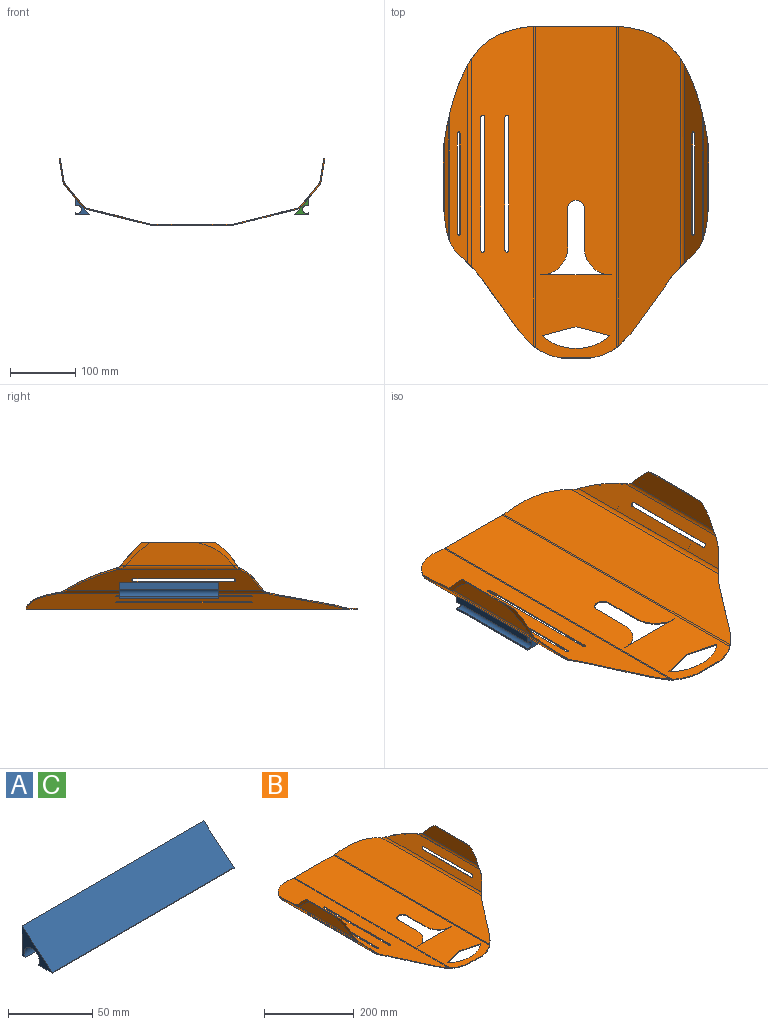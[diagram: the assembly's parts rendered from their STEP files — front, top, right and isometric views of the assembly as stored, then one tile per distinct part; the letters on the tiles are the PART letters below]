
ASSEMBLY  parts=3 mates=2
PART A: 8 faces, bbox 152.4x25.4x21.7 mm
  f0: plane 152.4x2.76mm, normal (0,0,-1), area 420mm2, adj f2,f5,f6,f7
  f1: plane 152.4x11.65mm, normal (0,0,-1), area 1774.8mm2, adj f4,f5,f6,f7
  f2: plane 152.4x21.72mm, normal (0,1,0), area 3310.1mm2, adj f0,f3,f5,f6
  f3: plane 152.4x25.4mm, normal (0,-0.64,0.77), area 5053.2mm2, adj f2,f4,f5,f6
  f4: plane 152.4x0.41mm, normal (0,-1,0), area 61.9mm2, adj f1,f3,f5,f6
  f5: plane 25.4x21.72mm, normal (1,0,0), area 179.1mm2, adj f0,f1,f2,f3,f4,f7
  f6: plane 25.4x21.72mm, normal (-1,0,0), area 179.1mm2, adj f0,f1,f2,f3,f4,f7
  f7: cylinder r=6.35mm len=152.4mm, axis (1,0,0), area 4053.7mm2, adj f0,f1,f5,f6
PART B: 60 faces, bbox 406.5x508.7x101.6 mm
  f0: plane 508.66x125.18mm, normal (0,0,-1), area 56761.7mm2, adj f16,f17,f18,f29,f30,f31,f32,f33
  f1: plane 508.66x125.18mm, normal (0,0,1), area 56761.7mm2, adj f6,f17,f28,f29,f30,f31,f32,f33
  f2: plane 298.37x32.29mm, normal (0.77,0,-0.64), area 9580.6mm2, adj f20,f21,f30,f32,f38,f39,f40,f41
  f3: plane 301.73x32.29mm, normal (-0.77,0,0.64), area 9787.3mm2, adj f25,f26,f30,f32,f38,f39,f40,f41
  f4: plane 301.73x32.29mm, normal (0.77,0,0.64), area 9787.3mm2, adj f8,f9,f31,f33,f34,f35,f36,f37
  f5: plane 298.37x32.29mm, normal (-0.77,0,-0.64), area 9580.6mm2, adj f13,f14,f31,f33,f34,f35,f36,f37
  f6: cylinder r=11.11mm len=491.86mm, axis (0,1,0), area 1338.6mm2, adj f1,f7,f31,f33
  f7: plane 489.51x95.87mm, normal (0.24,0,0.97), area 38384.7mm2, adj f6,f8,f31,f33,f52,f53,f54,f55
  f8: cylinder r=11.11mm len=316.99mm, axis (0,1,0), area 2156.1mm2, adj f4,f7,f31,f33
  f9: cylinder r=11.11mm len=194.91mm, axis (0,1,0), area 1096.4mm2, adj f4,f10,f31,f33
  f10: plane 177.21x34.42mm, normal (0.99,0,0.16), area 5197.5mm2, adj f9,f11,f31,f33
  f11: plane 112.31x1.72mm, normal (0,0,1), area 152.9mm2, adj f10,f12,f31,f33
  f12: plane 163.81x34.68mm, normal (-0.99,0,-0.16), area 4502.2mm2, adj f11,f13,f31,f33
  f13: cylinder r=12.7mm len=186.54mm, axis (0,1,0), area 1173.8mm2, adj f5,f12,f31,f33
  f14: cylinder r=12.7mm len=316.01mm, axis (0,1,0), area 2446.8mm2, adj f5,f15,f31,f33
  f15: plane 489.15x95.87mm, normal (-0.24,0,-0.97), area 38315.9mm2, adj f14,f16,f31,f33,f52,f53,f54,f55
  f16: cylinder r=12.7mm len=491.86mm, axis (0,1,0), area 1529.3mm2, adj f0,f15,f31,f33
  f17: plane 44.52x1.59mm, normal (0,-1,0), area 70.7mm2, adj f0,f1,f32,f33
  f18: cylinder r=12.7mm len=491.86mm, axis (0,1,0), area 1529.3mm2, adj f0,f19,f30,f32
  f19: plane 489.15x95.87mm, normal (0.24,0,-0.97), area 40960mm2, adj f18,f20,f30,f32
  f20: cylinder r=12.7mm len=316.01mm, axis (0,1,0), area 2446.8mm2, adj f2,f19,f30,f32
  f21: cylinder r=12.7mm len=186.54mm, axis (0,1,0), area 1173.8mm2, adj f2,f22,f30,f32
  f22: plane 163.81x34.68mm, normal (0.99,0,-0.16), area 4502.2mm2, adj f21,f23,f30,f32
  f23: plane 112.31x1.72mm, normal (0,0,1), area 152.9mm2, adj f22,f24,f30,f32
  f24: plane 177.21x34.42mm, normal (-0.99,0,0.16), area 5197.5mm2, adj f23,f25,f30,f32
  f25: cylinder r=11.11mm len=194.91mm, axis (0,1,0), area 1096.4mm2, adj f3,f24,f30,f32
  f26: cylinder r=11.11mm len=316.99mm, axis (0,1,0), area 2156.1mm2, adj f3,f27,f30,f32
  f27: plane 489.51x95.87mm, normal (-0.24,0,0.97), area 41028.7mm2, adj f26,f28,f30,f32
  f28: cylinder r=11.11mm len=491.86mm, axis (0,1,0), area 1338.6mm2, adj f1,f27,f30,f32
  f29: plane 121.22x1.59mm, normal (0,1,0), area 192.4mm2, adj f0,f1,f30,f31
  f30: extruded ~189.8x142.59mm, area 795.1mm2, adj f0,f1,f2,f3,f18,f19,f20,f21
  f31: extruded ~189.8x142.59mm, area 795.1mm2, adj f0,f1,f4,f5,f6,f7,f8,f9
  f32: extruded ~244.32x180.94mm, area 892.9mm2, adj f0,f1,f2,f3,f17,f18,f19,f20
  f33: extruded ~244.32x180.94mm, area 892.9mm2, adj f0,f1,f4,f5,f6,f7,f8,f9
  f34: plane 152.4x1.22mm, normal (-0.64,0,0.77), area 241.9mm2, adj f4,f5,f35,f37
  f35: cylinder r=3.17mm len=5.89mm, axis (-0.77,0,-0.64), area 15.8mm2, adj f4,f5,f34,f36
  f36: plane 152.4x1.22mm, normal (0.64,0,-0.77), area 241.9mm2, adj f4,f5,f35,f37
  f37: cylinder r=3.17mm len=5.89mm, axis (-0.77,0,-0.64), area 15.8mm2, adj f4,f5,f34,f36
  f38: plane 152.4x1.22mm, normal (0.64,0,0.77), area 241.9mm2, adj f2,f3,f39,f41
  f39: cylinder r=3.17mm len=5.89mm, axis (0.77,0,-0.64), area 15.8mm2, adj f2,f3,f38,f40
  f40: plane 152.4x1.22mm, normal (-0.64,0,-0.77), area 241.9mm2, adj f2,f3,f39,f41
  f41: cylinder r=3.17mm len=5.89mm, axis (0.77,0,-0.64), area 15.8mm2, adj f2,f3,f38,f40
  f42: plane 60.3x1.59mm, normal (1,0,0), area 95.7mm2, adj f0,f1,f43,f47
  f43: cylinder r=12.7mm len=25.4mm, axis (0,0,-1), area 63.3mm2, adj f0,f1,f42,f44
  f44: plane 59.7x1.59mm, normal (-1,0,0), area 94.8mm2, adj f0,f1,f43,f45
  f45: cylinder r=41.6mm len=41.9mm, axis (0,0,-1), area 104.2mm2, adj f0,f1,f44,f46
  f46: plane 108.6x1.59mm, normal (0,1,0), area 172.4mm2, adj f0,f1,f45,f47
  f47: cylinder r=41.6mm len=41.6mm, axis (0,0,-1), area 103.3mm2, adj f0,f1,f42,f46
  f48: plane 51.54x13.65mm, normal (-0.26,-0.97,0), area 84.6mm2, adj f0,f1,f49,f51
  f49: cylinder r=73.73mm len=51.54mm, axis (0,0,-1), area 89.7mm2, adj f0,f1,f48,f50
  f50: cylinder r=73.73mm len=51.54mm, axis (0,0,-1), area 89.7mm2, adj f0,f1,f49,f51
  f51: plane 51.54x13.65mm, normal (0.26,-0.97,0), area 84.6mm2, adj f0,f1,f48,f50
  f52: cylinder r=3.17mm len=6.55mm, axis (-0.24,0,-0.97), area 15.8mm2, adj f7,f15,f53,f55
  f53: plane 203.2x1.54mm, normal (0.97,0,-0.24), area 322.6mm2, adj f7,f15,f52,f54
  f54: cylinder r=3.17mm len=6.55mm, axis (-0.24,0,-0.97), area 15.8mm2, adj f7,f15,f53,f55
  f55: plane 203.2x1.54mm, normal (-0.97,0,0.24), area 322.6mm2, adj f7,f15,f52,f54
  f56: plane 203.2x1.54mm, normal (-0.97,0,0.24), area 322.6mm2, adj f7,f15,f57,f59
  f57: cylinder r=3.17mm len=6.55mm, axis (-0.24,0,-0.97), area 15.8mm2, adj f7,f15,f56,f58
  f58: plane 203.2x1.54mm, normal (0.97,0,-0.24), area 322.6mm2, adj f7,f15,f57,f59
  f59: cylinder r=3.17mm len=6.55mm, axis (-0.24,0,-0.97), area 15.8mm2, adj f7,f15,f56,f58
PART C: same geometry as A
PLACE A rot(axis=(-0.58,0.58,-0.58),120deg) t=(-178.86,-142.41,16.18)mm
PLACE B at identity fixed
PLACE C rot(axis=(-0.58,-0.58,0.58),120deg) t=(178.86,-294.81,16.18)mm
MATE fastened B.f2 <-> C.f3  axis (0.77,0,-0.64) through (180.05,-218.61,43.47)mm
MATE fastened B.f5 <-> A.f3  axis (-0.77,0,-0.64) through (-180.05,-218.61,43.47)mm
